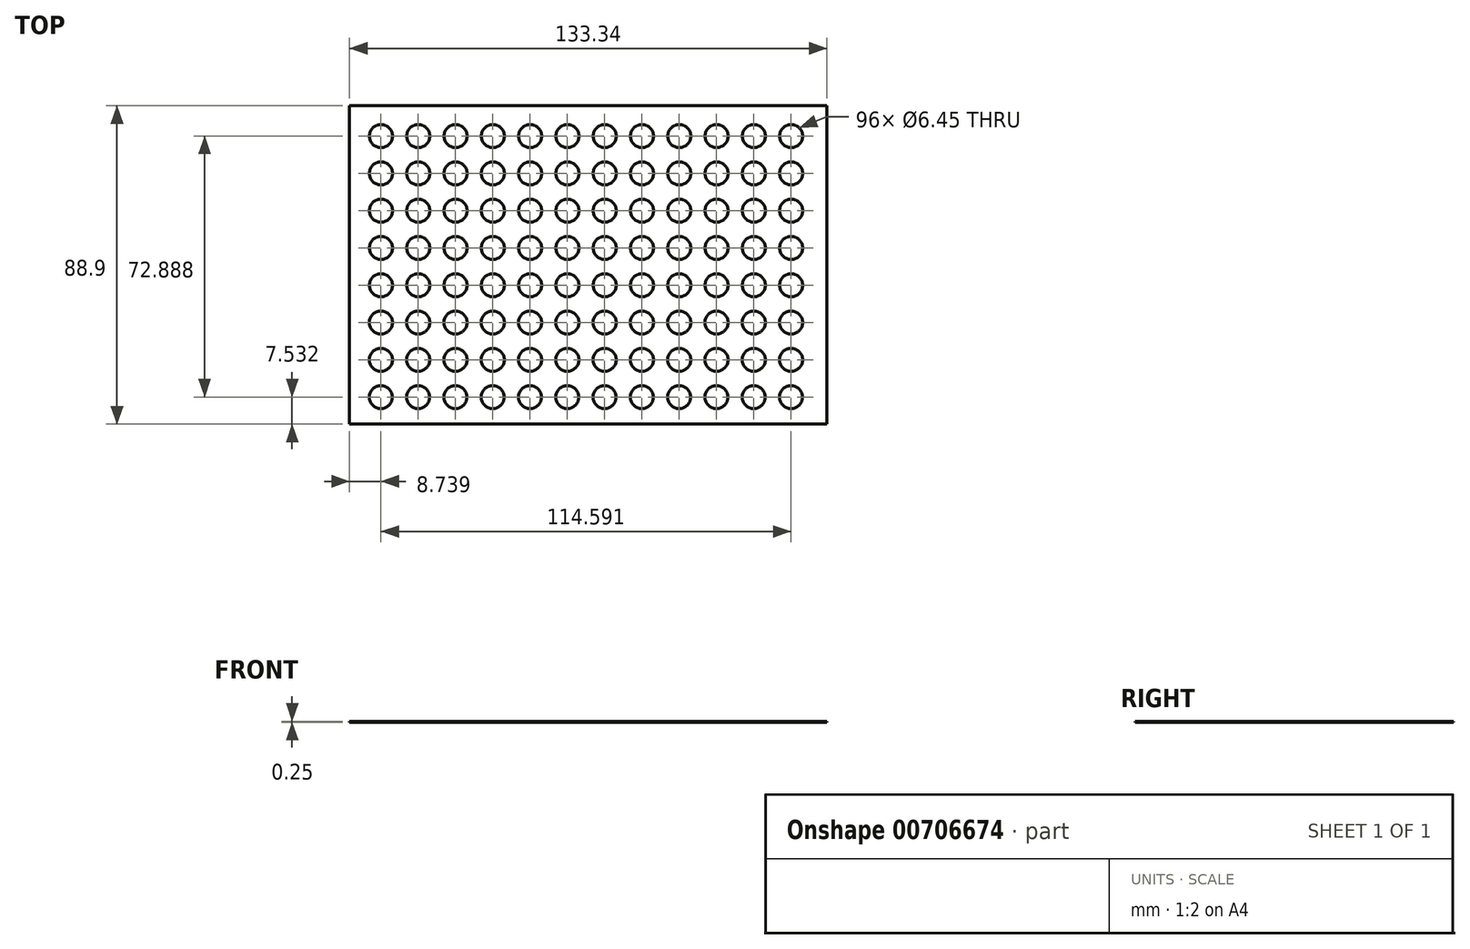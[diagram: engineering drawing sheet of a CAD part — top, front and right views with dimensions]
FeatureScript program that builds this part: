
annotation { "Feature Type Name" : "Feature", "Feature Type Description" : "" }
export const myFeature = defineFeature(function(context is Context, id is Id, definition is map)
    precondition{}
    {
        {
            var Q0;
            Q0=qCreatedBy(makeId("Top.planeOp"),FACE);
            var sketch = newSketch(context, id + "F0", { "sketchPlane" : qUnion([Q0])});
            skLineSegment(sketch, "E0.bottom", {"start": v(-66.67, 44.45) * mm, "end": v(66.68, 44.45) * mm});
            skLineSegment(sketch, "E0.top", {"start": v(-66.68, -44.45) * mm, "end": v(66.68, -44.45) * mm});
            skLineSegment(sketch, "E0.left", {"start": v(-66.67, 44.45) * mm, "end": v(-66.68, -44.45) * mm});
            skLineSegment(sketch, "E0.right", {"start": v(66.68, 44.45) * mm, "end": v(66.68, -44.45) * mm});
            skPoint(sketch, "E0.middle", {"position": v(0, 0) * mm});
            skSolve(sketch);
        }
        {
            var Q0;
            Q0=makeQuery(id+"F0.imprint","IMPRINT",FACE,{"disambiguationData":[TD([[makeQuery(id+"F0.imprint","IMPRINT",EDGE,{"derivedFrom":sQuery(id+"F0.wireOp",EDGE,"E0.bottom")}),-1.0]])]});
            var sketch = newSketch(context, id + "F1", { "sketchPlane" : qUnion([Q0])});
            skCircle(sketch, "E1", {"center": v(-57.9, 35.97) * mm, "radius": 3.23 * mm});
            skCircle(sketch, "E2.1.0.0", {"center": v(-47.48, 35.97) * mm, "radius": 3.23 * mm});
            skCircle(sketch, "E2.2.0.0", {"center": v(-37.07, 35.97) * mm, "radius": 3.23 * mm});
            skCircle(sketch, "E2.3.0.0", {"center": v(-26.65, 35.97) * mm, "radius": 3.23 * mm});
            skCircle(sketch, "E2.4.0.0", {"center": v(-16.24, 35.97) * mm, "radius": 3.23 * mm});
            skCircle(sketch, "E2.5.0.0", {"center": v(-5.82, 35.97) * mm, "radius": 3.23 * mm});
            skCircle(sketch, "E2.6.0.0", {"center": v(4.59, 35.97) * mm, "radius": 3.23 * mm});
            skCircle(sketch, "E2.7.0.0", {"center": v(15, 35.97) * mm, "radius": 3.23 * mm});
            skCircle(sketch, "E2.8.0.0", {"center": v(25.42, 35.97) * mm, "radius": 3.23 * mm});
            skCircle(sketch, "E2.9.0.0", {"center": v(35.83, 35.97) * mm, "radius": 3.23 * mm});
            skCircle(sketch, "E2.10.0.0", {"center": v(46.25, 35.97) * mm, "radius": 3.23 * mm});
            skCircle(sketch, "E2.11.0.0", {"center": v(56.66, 35.97) * mm, "radius": 3.23 * mm});
            skLineSegment(sketch, "E2.direction1", {"start": v(-57.9, 35.97) * mm, "end": v(-57.9, 25.56) * mm, "construction": true});
            skSolve(sketch);
        }
        {
            var Q0;
            Q0=qCreatedBy(makeId("Top.planeOp"),FACE);
            var sketch = newSketch(context, id + "F2", { "sketchPlane" : qUnion([Q0])});
            skCircle(sketch, "E3", {"center": v(-57.9, 25.55) * mm, "radius": 3.23 * mm});
            skCircle(sketch, "E4.1.0.0", {"center": v(-47.48, 25.55) * mm, "radius": 3.23 * mm});
            skCircle(sketch, "E4.2.0.0", {"center": v(-37.07, 25.55) * mm, "radius": 3.23 * mm});
            skCircle(sketch, "E4.3.0.0", {"center": v(-26.65, 25.55) * mm, "radius": 3.23 * mm});
            skCircle(sketch, "E4.4.0.0", {"center": v(-16.24, 25.55) * mm, "radius": 3.23 * mm});
            skCircle(sketch, "E4.5.0.0", {"center": v(-5.82, 25.55) * mm, "radius": 3.23 * mm});
            skCircle(sketch, "E4.6.0.0", {"center": v(4.59, 25.55) * mm, "radius": 3.23 * mm});
            skCircle(sketch, "E4.7.0.0", {"center": v(15, 25.55) * mm, "radius": 3.23 * mm});
            skCircle(sketch, "E4.8.0.0", {"center": v(25.42, 25.55) * mm, "radius": 3.23 * mm});
            skCircle(sketch, "E4.9.0.0", {"center": v(35.83, 25.55) * mm, "radius": 3.23 * mm});
            skCircle(sketch, "E4.10.0.0", {"center": v(46.25, 25.55) * mm, "radius": 3.23 * mm});
            skCircle(sketch, "E4.11.0.0", {"center": v(56.66, 25.55) * mm, "radius": 3.23 * mm});
            skLineSegment(sketch, "E4.direction1", {"start": v(-57.9, 25.55) * mm, "end": v(-57.9, 15.14) * mm, "construction": true});
            skSolve(sketch);
        }
        {
            var Q0;
            Q0=qCreatedBy(makeId("Top.planeOp"),FACE);
            var sketch = newSketch(context, id + "F3", { "sketchPlane" : qUnion([Q0])});
            skCircle(sketch, "E5", {"center": v(-57.9, 15.14) * mm, "radius": 3.23 * mm});
            skCircle(sketch, "E6.1.0.0", {"center": v(-47.48, 15.14) * mm, "radius": 3.23 * mm});
            skCircle(sketch, "E6.2.0.0", {"center": v(-37.07, 15.14) * mm, "radius": 3.23 * mm});
            skCircle(sketch, "E6.3.0.0", {"center": v(-26.65, 15.14) * mm, "radius": 3.23 * mm});
            skCircle(sketch, "E6.4.0.0", {"center": v(-16.24, 15.14) * mm, "radius": 3.23 * mm});
            skCircle(sketch, "E6.5.0.0", {"center": v(-5.82, 15.14) * mm, "radius": 3.23 * mm});
            skCircle(sketch, "E6.6.0.0", {"center": v(4.59, 15.14) * mm, "radius": 3.23 * mm});
            skCircle(sketch, "E6.7.0.0", {"center": v(15, 15.14) * mm, "radius": 3.23 * mm});
            skCircle(sketch, "E6.8.0.0", {"center": v(25.42, 15.14) * mm, "radius": 3.23 * mm});
            skCircle(sketch, "E6.9.0.0", {"center": v(35.83, 15.14) * mm, "radius": 3.23 * mm});
            skCircle(sketch, "E6.10.0.0", {"center": v(46.25, 15.14) * mm, "radius": 3.23 * mm});
            skCircle(sketch, "E6.11.0.0", {"center": v(56.66, 15.14) * mm, "radius": 3.23 * mm});
            skLineSegment(sketch, "E6.direction1", {"start": v(-57.9, 15.14) * mm, "end": v(-57.9, 4.73) * mm, "construction": true});
            skSolve(sketch);
        }
        {
            var Q0;
            Q0=qCreatedBy(makeId("Top.planeOp"),FACE);
            var sketch = newSketch(context, id + "F4", { "sketchPlane" : qUnion([Q0])});
            skCircle(sketch, "E7", {"center": v(-57.9, 4.74) * mm, "radius": 3.23 * mm});
            skCircle(sketch, "E8.1.0.0", {"center": v(-47.48, 4.74) * mm, "radius": 3.23 * mm});
            skCircle(sketch, "E8.2.0.0", {"center": v(-37.07, 4.74) * mm, "radius": 3.23 * mm});
            skCircle(sketch, "E8.3.0.0", {"center": v(-26.65, 4.74) * mm, "radius": 3.23 * mm});
            skCircle(sketch, "E8.4.0.0", {"center": v(-16.24, 4.74) * mm, "radius": 3.23 * mm});
            skCircle(sketch, "E8.5.0.0", {"center": v(-5.83, 4.74) * mm, "radius": 3.23 * mm});
            skCircle(sketch, "E8.6.0.0", {"center": v(4.59, 4.74) * mm, "radius": 3.23 * mm});
            skCircle(sketch, "E8.7.0.0", {"center": v(15, 4.74) * mm, "radius": 3.23 * mm});
            skCircle(sketch, "E8.8.0.0", {"center": v(25.42, 4.74) * mm, "radius": 3.23 * mm});
            skCircle(sketch, "E8.9.0.0", {"center": v(35.83, 4.74) * mm, "radius": 3.23 * mm});
            skCircle(sketch, "E8.10.0.0", {"center": v(46.24, 4.74) * mm, "radius": 3.23 * mm});
            skCircle(sketch, "E8.11.0.0", {"center": v(56.66, 4.74) * mm, "radius": 3.23 * mm});
            skLineSegment(sketch, "E8.direction1", {"start": v(-57.9, 4.74) * mm, "end": v(-57.9, -5.68) * mm, "construction": true});
            skSolve(sketch);
        }
        {
            var Q0;
            Q0=makeQuery(id+"F1.imprint","IMPRINT",FACE,{"disambiguationData":[TD([[makeQuery(id+"F1.imprint","IMPRINT",EDGE,{"derivedFrom":sQuery(id+"F1.wireOp",EDGE,"E1")}),-1.0]])]});
            var sketch = newSketch(context, id + "F5", { "sketchPlane" : qUnion([Q0])});
            skCircle(sketch, "E9", {"center": v(-57.9, -5.68) * mm, "radius": 3.23 * mm});
            skLineSegment(sketch, "E10.direction1", {"start": v(-57.9, -5.68) * mm, "end": v(-57.9, -16.1) * mm, "construction": true});
            skCircle(sketch, "E11.0.1.0", {"center": v(-57.9, -16.1) * mm, "radius": 3.23 * mm});
            skCircle(sketch, "E11.0.2.0", {"center": v(-57.92, -26.5) * mm, "radius": 3.23 * mm});
            skCircle(sketch, "E11.0.3.0", {"center": v(-57.93, -36.92) * mm, "radius": 3.23 * mm});
            skCircle(sketch, "E11.1.0.0", {"center": v(-47.48, -5.68) * mm, "radius": 3.23 * mm});
            skCircle(sketch, "E11.1.1.0", {"center": v(-47.5, -16.1) * mm, "radius": 3.23 * mm});
            skCircle(sketch, "E11.1.2.0", {"center": v(-47.5, -26.5) * mm, "radius": 3.23 * mm});
            skCircle(sketch, "E11.1.3.0", {"center": v(-47.52, -36.92) * mm, "radius": 3.23 * mm});
            skCircle(sketch, "E11.2.0.0", {"center": v(-37.07, -5.68) * mm, "radius": 3.23 * mm});
            skCircle(sketch, "E11.2.1.0", {"center": v(-37.08, -16.1) * mm, "radius": 3.23 * mm});
            skCircle(sketch, "E11.2.2.0", {"center": v(-37.1, -26.5) * mm, "radius": 3.23 * mm});
            skCircle(sketch, "E11.2.3.0", {"center": v(-37.1, -36.92) * mm, "radius": 3.23 * mm});
            skCircle(sketch, "E11.3.0.0", {"center": v(-26.66, -5.68) * mm, "radius": 3.23 * mm});
            skCircle(sketch, "E11.3.1.0", {"center": v(-26.67, -16.1) * mm, "radius": 3.23 * mm});
            skCircle(sketch, "E11.3.2.0", {"center": v(-26.68, -26.5) * mm, "radius": 3.23 * mm});
            skCircle(sketch, "E11.3.3.0", {"center": v(-26.69, -36.92) * mm, "radius": 3.23 * mm});
            skCircle(sketch, "E11.4.0.0", {"center": v(-16.24, -5.68) * mm, "radius": 3.23 * mm});
            skCircle(sketch, "E11.4.1.0", {"center": v(-16.25, -16.1) * mm, "radius": 3.23 * mm});
            skCircle(sketch, "E11.4.2.0", {"center": v(-16.26, -26.5) * mm, "radius": 3.23 * mm});
            skCircle(sketch, "E11.4.3.0", {"center": v(-16.28, -36.92) * mm, "radius": 3.23 * mm});
            skCircle(sketch, "E11.5.0.0", {"center": v(-5.83, -5.68) * mm, "radius": 3.23 * mm});
            skCircle(sketch, "E11.5.1.0", {"center": v(-5.84, -16.1) * mm, "radius": 3.23 * mm});
            skCircle(sketch, "E11.5.2.0", {"center": v(-5.85, -26.5) * mm, "radius": 3.23 * mm});
            skCircle(sketch, "E11.5.3.0", {"center": v(-5.86, -36.92) * mm, "radius": 3.23 * mm});
            skCircle(sketch, "E11.6.0.0", {"center": v(4.59, -5.68) * mm, "radius": 3.23 * mm});
            skCircle(sketch, "E11.6.1.0", {"center": v(4.58, -16.1) * mm, "radius": 3.23 * mm});
            skCircle(sketch, "E11.6.2.0", {"center": v(4.56, -26.5) * mm, "radius": 3.23 * mm});
            skCircle(sketch, "E11.6.3.0", {"center": v(4.55, -36.92) * mm, "radius": 3.23 * mm});
            skCircle(sketch, "E11.7.0.0", {"center": v(15, -5.68) * mm, "radius": 3.23 * mm});
            skCircle(sketch, "E11.7.1.0", {"center": v(14.99, -16.1) * mm, "radius": 3.23 * mm});
            skCircle(sketch, "E11.7.2.0", {"center": v(14.98, -26.5) * mm, "radius": 3.23 * mm});
            skCircle(sketch, "E11.7.3.0", {"center": v(14.97, -36.92) * mm, "radius": 3.23 * mm});
            skCircle(sketch, "E11.8.0.0", {"center": v(25.41, -5.68) * mm, "radius": 3.23 * mm});
            skCircle(sketch, "E11.8.1.0", {"center": v(25.4, -16.1) * mm, "radius": 3.23 * mm});
            skCircle(sketch, "E11.8.2.0", {"center": v(25.4, -26.5) * mm, "radius": 3.23 * mm});
            skCircle(sketch, "E11.8.3.0", {"center": v(25.38, -36.92) * mm, "radius": 3.23 * mm});
            skCircle(sketch, "E11.9.0.0", {"center": v(35.83, -5.68) * mm, "radius": 3.23 * mm});
            skCircle(sketch, "E11.9.1.0", {"center": v(35.82, -16.1) * mm, "radius": 3.23 * mm});
            skCircle(sketch, "E11.9.2.0", {"center": v(35.8, -26.5) * mm, "radius": 3.23 * mm});
            skCircle(sketch, "E11.9.3.0", {"center": v(35.8, -36.92) * mm, "radius": 3.23 * mm});
            skCircle(sketch, "E11.10.0.0", {"center": v(46.24, -5.68) * mm, "radius": 3.23 * mm});
            skCircle(sketch, "E11.10.1.0", {"center": v(46.23, -16.1) * mm, "radius": 3.23 * mm});
            skCircle(sketch, "E11.10.2.0", {"center": v(46.22, -26.5) * mm, "radius": 3.23 * mm});
            skCircle(sketch, "E11.10.3.0", {"center": v(46.2, -36.92) * mm, "radius": 3.23 * mm});
            skCircle(sketch, "E11.11.0.0", {"center": v(56.66, -5.68) * mm, "radius": 3.23 * mm});
            skCircle(sketch, "E11.11.1.0", {"center": v(56.65, -16.1) * mm, "radius": 3.23 * mm});
            skCircle(sketch, "E11.11.2.0", {"center": v(56.63, -26.5) * mm, "radius": 3.23 * mm});
            skCircle(sketch, "E11.11.3.0", {"center": v(56.62, -36.92) * mm, "radius": 3.23 * mm});
            skLineSegment(sketch, "E11.direction1", {"start": v(-57.9, -5.68) * mm, "end": v(-47.48, -5.68) * mm, "construction": true});
            skSolve(sketch);
        }
        {
            var Q0;
            Q0=makeQuery(id+"F0.imprint","IMPRINT",FACE,{"disambiguationData":[TD([[makeQuery(id+"F0.imprint","IMPRINT",EDGE,{"derivedFrom":sQuery(id+"F0.wireOp",EDGE,"E0.bottom")}),-1.0]])]});
            extrude(context, id + "F6", {"entities" : qUnion([Q0]), "depth" : 0.25 * mm, "offsetDistance" : 25.4 * mm});
        }
        {
            var Q0;
            Q0=qSketchRegion(id+"F1",true);
            var Q1;
            Q1=qSketchRegion(id+"F2",true);
            var Q2;
            Q2=qSketchRegion(id+"F3",true);
            var Q3;
            Q3=qSketchRegion(id+"F4",true);
            var Q4;
            Q4=qSketchRegion(id+"F5",true);
            extrude(context, id + "F7", {"entities" : qUnion([Q0, Q1, Q2, Q3, Q4]), "operationType" : NewBodyOperationType.REMOVE, "depth" : 0.25 * mm, "offsetDistance" : 25.4 * mm});
        }
    });
